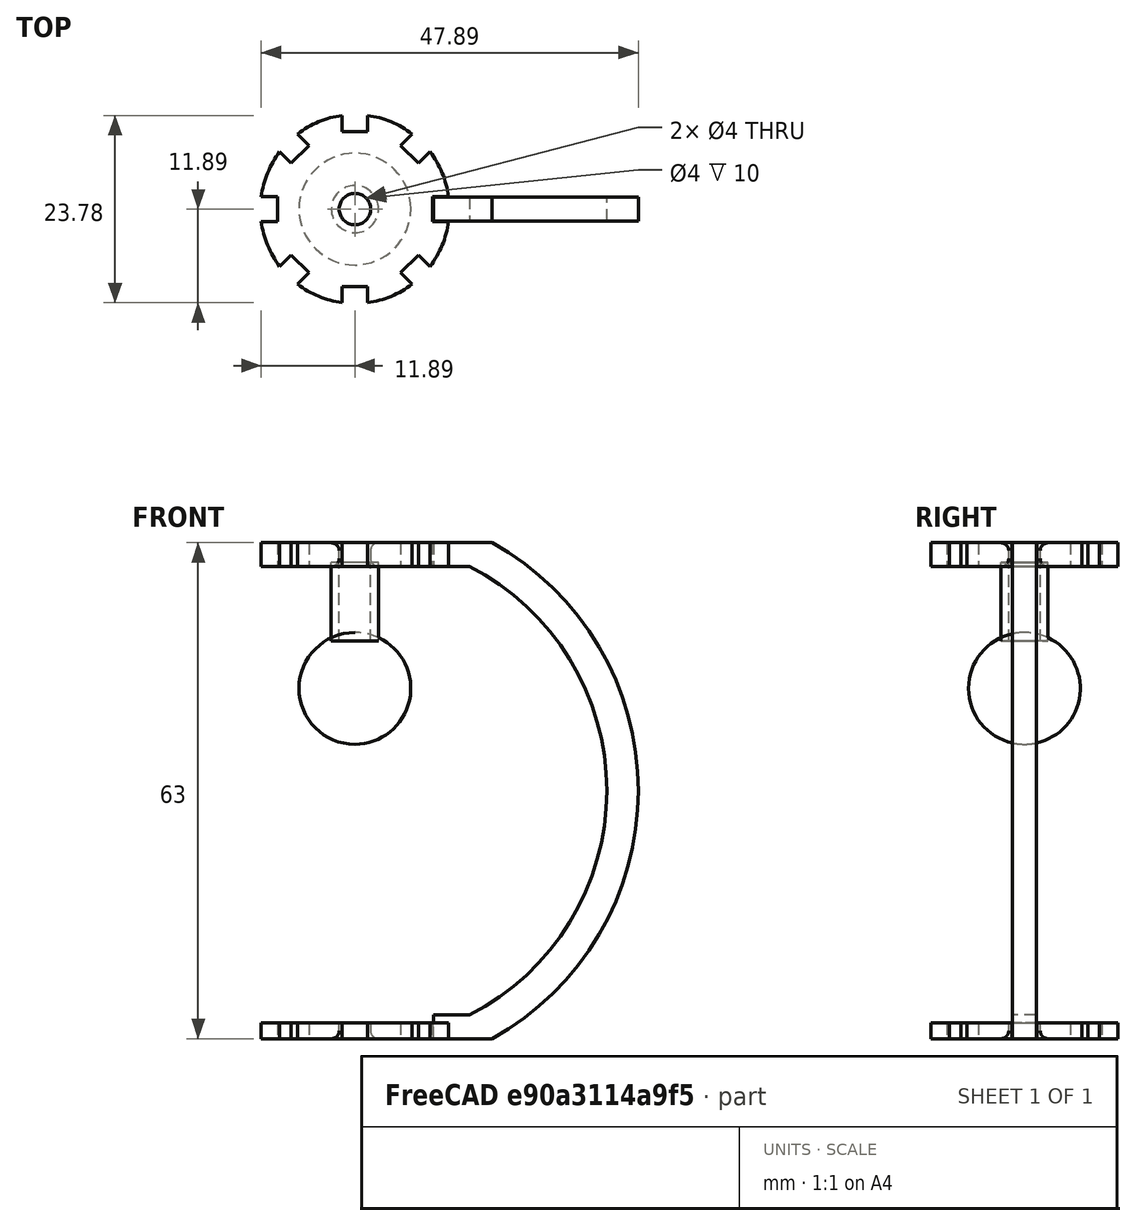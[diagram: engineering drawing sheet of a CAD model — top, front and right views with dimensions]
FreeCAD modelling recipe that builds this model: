
FCSTD DOCUMENT  (FreeCAD 0.19R)
Label: Lamp shade
License: All rights reserved
LicenseURL: http://en.wikipedia.org/wiki/All_rights_reserved
objects: TechDraw::DrawViewDimension×14, TechDraw::DrawProjGroupItem×9, Sketcher::SketchObject×7, PartDesign::Pocket×4, PartDesign::Pad×3, PartDesign::Body×3, PartDesign::Fillet×3, TechDraw::DrawSVGTemplate×2, TechDraw::DrawProjGroup×2, TechDraw::DrawViewSymbol×2, TechDraw::DrawPage×2, PartDesign::PolarPattern×2, Part::FeaturePython×2, TechDraw::DrawViewPart×1, Part::Sphere×1, Part::Compound×1
note: 35 computed .brp shape members not serialized (recipe doc carries the construction recipe); baked Part::Feature solids carry a one-line shape summary decoded from their .brp

FEATURE [Sketcher::SketchObject] Sketch
  FullyConstrained = false
  MapMode = 5
  Placement = pos=(0,0,0) rot=(1,0,0;1.5708rad)
  Support = -> [XZ_Plane]
  sketch-geometry (11):
    g0: LineSegment StartX=0 StartY=31.5 StartZ=0 EndX=10 EndY=31.5 EndZ=0
    g1: LineSegment StartX=0 StartY=-31.5 StartZ=0 EndX=10 EndY=-31.5 EndZ=0
    g2: LineSegment StartX=10 StartY=31.5 StartZ=0 EndX=10 EndY=28.5 EndZ=0
    g3: LineSegment StartX=10 StartY=-31.5 StartZ=0 EndX=10 EndY=-28.5 EndZ=0
    g4: ArcOfCircle CenterX=0 CenterY=0 CenterZ=0 NormalX=0 NormalY=0 NormalZ=1 AngleXU=0 Radius=36 StartAngle=5.21775 EndAngle=7.34862
    g5: LineSegment StartX=10 StartY=31.5 StartZ=0 EndX=17.4284 EndY=31.5 EndZ=0
    g6: LineSegment StartX=17.4284 StartY=-31.5 StartZ=0 EndX=10 EndY=-31.5 EndZ=0
    g7: ArcOfCircle CenterX=0 CenterY=0 CenterZ=0 NormalX=0 NormalY=0 NormalZ=1 AngleXU=0 Radius=32 StartAngle=5.18447 EndAngle=7.3819
    g8: LineSegment StartX=10 StartY=28.5 StartZ=0 EndX=14.5516 EndY=28.5 EndZ=0
    g9: LineSegment StartX=10 StartY=-28.5 StartZ=0 EndX=14.5516 EndY=-28.5 EndZ=0
    g10: LineSegment StartX=0 StartY=15.8658 StartZ=0 EndX=0 EndY=-16.2724 EndZ=0
  constraints (31):
    c: PointOnObject(g0,g-2)
    c: Horizontal(g0)
    c: Horizontal(g1)
    c: DistanceY(g1,g0) = 63
    c: Symmetric(g0,g1,g-1)
    c: DistanceX(g0,g0) = 10
    c: Equal(g1,g0)
    c: Coincident(g2,g0)
    c: Vertical(g2)
    c: Coincident(g3,g1)
    c: Vertical(g3)
    c: Coincident(g5,g2)
    c: Coincident(g5,g4)
    c: Horizontal(g5)
    c: Coincident(g6,g4)
    c: Coincident(g6,g3)
    c: Horizontal(g6)
    c: Coincident(g8,g2)
    c: Coincident(g8,g7)
    c: Coincident(g9,g3)
    c: Coincident(g9,g7)
    c: Horizontal(g9)
    c: Horizontal(g8)
    c: DistanceY(g2,g2) = 3
    c: Equal(g2,g3)
    c: Coincident(g4,g-1)
    c: Coincident(g7,g4)
    c: Radius(g7) = 32
    c: Radius(g4) = 36
    c: PointOnObject(g10,g-2)
    c: Vertical(g10)
FEATURE [PartDesign::Pad] Pad
  Direction = (1,1,1)
  Length = 3
  Length2 = 100
  Midplane = true
  Placement = pos=(0,0,0) rot=(1,0,0;1.5708rad)
  Profile = -> Sketch
  Type = 0
FEATURE [PartDesign::Body] Body  label="Fins"
  Group = -> [Sketch,Pad]
  Origin = -> Origin
  Tip = -> Pad
FEATURE [TechDraw::DrawSVGTemplate] Template
  EditableTexts = Designed_by_Name=MD Harrington; Drawing_number=Drawing number; FC-Date=14/12/22; FC-SC=1:3; FC-SH=Sheet; FC-Title=Title; Subtitle=Light Shade Fins; Weight=Weight
  Height = 210
  Orientation = 1
  Width = 297
FEATURE [TechDraw::DrawProjGroupItem] ProjItem  label="Front"
  CoarseView = false
  Direction = (0,-1,0)
  Focus = 100
  HardHidden = false
  IsoCount = 0
  IsoHidden = false
  IsoVisible = false
  LockPosition = true
  Perspective = false
  Rotation = 0
  RotationVector = (1,0,0)
  ScaleType = 2
  SeamHidden = false
  SeamVisible = true
  SmoothHidden = false
  SmoothVisible = true
  Source = -> [Pad]
  Type = 0
  X = 0
  XDirection = (1,0,0)
  Y = 0
FEATURE [TechDraw::DrawProjGroupItem] ProjItem001  label="Bottom"
  CoarseView = false
  Direction = (0,0,-1)
  Focus = 100
  HardHidden = false
  IsoCount = 0
  IsoHidden = false
  IsoVisible = false
  LockPosition = false
  Perspective = false
  Rotation = 0
  RotationVector = (1,0,0)
  ScaleType = 2
  SeamHidden = false
  SeamVisible = true
  SmoothHidden = false
  SmoothVisible = true
  Source = -> [Pad]
  Type = 5
  X = 0
  XDirection = (1,0,0)
  Y = 65
FEATURE [TechDraw::DrawProjGroupItem] ProjItem002  label="Right"
  CoarseView = false
  Direction = (1,-1e-16,0)
  Focus = 100
  HardHidden = false
  IsoCount = 0
  IsoHidden = false
  IsoVisible = false
  LockPosition = false
  Perspective = false
  Rotation = 0
  RotationVector = (1,0,0)
  ScaleType = 2
  SeamHidden = false
  SeamVisible = true
  SmoothHidden = false
  SmoothVisible = true
  Source = -> [Pad]
  Type = 2
  X = -54.5
  XDirection = (1e-16,1,0)
  Y = 0
FEATURE [TechDraw::DrawProjGroupItem] ProjItem003  label="Left"
  CoarseView = false
  Direction = (-1,-1e-16,0)
  Focus = 100
  HardHidden = false
  IsoCount = 0
  IsoHidden = false
  IsoVisible = false
  LockPosition = false
  Perspective = false
  Rotation = 0
  RotationVector = (1,0,0)
  ScaleType = 2
  SeamHidden = false
  SeamVisible = true
  SmoothHidden = false
  SmoothVisible = true
  Source = -> [Pad]
  Type = 1
  X = 54.5
  XDirection = (1e-16,-1,0)
  Y = 0
FEATURE [TechDraw::DrawProjGroupItem] ProjItem004  label="Rear"
  CoarseView = false
  Direction = (0,1,0)
  Focus = 100
  HardHidden = false
  IsoCount = 0
  IsoHidden = false
  IsoVisible = false
  LockPosition = false
  Perspective = false
  Rotation = 0
  RotationVector = (1,0,0)
  ScaleType = 2
  SeamHidden = false
  SeamVisible = true
  SmoothHidden = false
  SmoothVisible = true
  Source = -> [Pad]
  Type = 3
  X = 120.5
  XDirection = (-1,0,0)
  Y = 0
FEATURE [TechDraw::DrawProjGroup] ProjGroup
  Anchor = -> ProjItem
  AutoDistribute = true
  LockPosition = false
  ProjectionType = 0
  Rotation = 0
  ScaleType = 0
  Source = -> [Pad]
  Views = -> [ProjItem,ProjItem001,ProjItem002,ProjItem003,ProjItem004]
  X = 122.234
  Y = 109.949
  spacingX = 40
  spacingY = 32
FEATURE [TechDraw::DrawViewDimension] Dimension
  Arbitrary = false
  ArbitraryTolerances = false
  EqualTolerance = true
  FormatSpec = %.2f
  FormatSpecOverTolerance = %+.2f
  FormatSpecUnderTolerance = %+.2f
  Inverted = false
  LockPosition = false
  MeasureType = 1
  OverTolerance = 0
  References2D = -> [ProjItem002]
  Rotation = 0
  ScaleType = 0
  TheoreticalExact = false
  Type = 2
  UnderTolerance = 0
  X = -29.0365
  Y = 0
FEATURE [TechDraw::DrawViewDimension] Dimension001
  Arbitrary = false
  ArbitraryTolerances = false
  EqualTolerance = true
  FormatSpec = %.2f
  FormatSpecOverTolerance = %+.2f
  FormatSpecUnderTolerance = %+.2f
  Inverted = false
  LockPosition = false
  MeasureType = 1
  OverTolerance = 0
  References2D = -> [ProjItem]
  Rotation = 0
  ScaleType = 0
  TheoreticalExact = false
  Type = 2
  UnderTolerance = 0
  X = -35.4698
  Y = -0.440584
FEATURE [TechDraw::DrawViewDimension] Dimension002
  Arbitrary = false
  ArbitraryTolerances = false
  EqualTolerance = true
  FormatSpec = %.2f
  FormatSpecOverTolerance = %+.2f
  FormatSpecUnderTolerance = %+.2f
  Inverted = false
  LockPosition = false
  MeasureType = 1
  OverTolerance = 0
  References2D = -> [ProjItem003]
  Rotation = 0
  ScaleType = 0
  TheoreticalExact = false
  Type = 2
  UnderTolerance = 0
  X = 16.4799
  Y = 11.4955
FEATURE [TechDraw::DrawViewDimension] Dimension003
  Arbitrary = false
  ArbitraryTolerances = false
  EqualTolerance = true
  FormatSpec = %.2f
  FormatSpecOverTolerance = %+.2f
  FormatSpecUnderTolerance = %+.2f
  Inverted = false
  LockPosition = false
  MeasureType = 1
  OverTolerance = 0
  References2D = -> [ProjItem003]
  Rotation = 0
  ScaleType = 0
  TheoreticalExact = false
  Type = 1
  UnderTolerance = 0
  X = -32.6032
  Y = 49.3437
FEATURE [TechDraw::DrawViewDimension] Dimension004
  Arbitrary = false
  ArbitraryTolerances = false
  EqualTolerance = true
  FormatSpec = %.2f
  FormatSpecOverTolerance = %+.2f
  FormatSpecUnderTolerance = %+.2f
  Inverted = false
  LockPosition = false
  MeasureType = 1
  OverTolerance = 0
  References2D = -> [ProjItem]
  Rotation = 0
  ScaleType = 0
  TheoreticalExact = false
  Type = 1
  UnderTolerance = 0
  X = -38.144
  Y = 48.6828
FEATURE [TechDraw::DrawViewDimension] Dimension005
  Arbitrary = false
  ArbitraryTolerances = false
  EqualTolerance = true
  FormatSpec = %.2f
  FormatSpecOverTolerance = %+.2f
  FormatSpecUnderTolerance = %+.2f
  Inverted = false
  LockPosition = false
  MeasureType = 1
  OverTolerance = 0
  References2D = -> [ProjItem]
  Rotation = 0
  ScaleType = 0
  TheoreticalExact = false
  Type = 1
  UnderTolerance = 0
  X = -23.0605
  Y = 4.98439
FEATURE [TechDraw::DrawViewDimension] Dimension006
  Arbitrary = false
  ArbitraryTolerances = false
  EqualTolerance = true
  FormatSpec = %.2f
  FormatSpecOverTolerance = %+.2f
  FormatSpecUnderTolerance = %+.2f
  Inverted = false
  LockPosition = false
  MeasureType = 1
  OverTolerance = 0
  References2D = -> [ProjItem001]
  Rotation = 0
  ScaleType = 0
  TheoreticalExact = false
  Type = 1
  UnderTolerance = 0
  X = -60.5803
  Y = 13.1755
FEATURE [TechDraw::DrawViewDimension] Dimension007
  Arbitrary = false
  ArbitraryTolerances = false
  EqualTolerance = true
  FormatSpec = R%.2f
  FormatSpecOverTolerance = %+.2f
  FormatSpecUnderTolerance = %+.2f
  Inverted = false
  LockPosition = false
  MeasureType = 1
  OverTolerance = 0
  References2D = -> [ProjItem004]
  Rotation = 0
  ScaleType = 0
  TheoreticalExact = false
  Type = 4
  UnderTolerance = 0
  X = -15.2002
  Y = 52.2092
FEATURE [TechDraw::DrawViewDimension] Dimension008
  Arbitrary = false
  ArbitraryTolerances = false
  EqualTolerance = true
  FormatSpec = R%.2f
  FormatSpecOverTolerance = %+.2f
  FormatSpecUnderTolerance = %+.2f
  Inverted = false
  LockPosition = false
  MeasureType = 1
  OverTolerance = 0
  References2D = -> [ProjItem004]
  Rotation = 0
  ScaleType = 0
  TheoreticalExact = false
  Type = 4
  UnderTolerance = 0
  X = -29.0785
  Y = -21.148
FEATURE [TechDraw::DrawViewPart] View
  CoarseView = false
  Direction = (0,-1,0)
  Focus = 100
  HardHidden = false
  IsoCount = 0
  IsoHidden = false
  IsoVisible = false
  LockPosition = false
  Perspective = false
  Rotation = 0
  ScaleType = 0
  SeamHidden = false
  SeamVisible = true
  SmoothHidden = false
  SmoothVisible = true
  Source = -> [Dimension008]
  X = 148.5
  XDirection = (1,0,0)
  Y = 105
FEATURE [TechDraw::DrawViewSymbol] ActiveView
  LockPosition = false
  Rotation = 0
  ScaleType = 2
  Symbol = <blob: 55645 chars omitted>
  X = 268.703
  Y = 156.462
FEATURE [TechDraw::DrawPage] Page  label="FinsTecDrawing"
  KeepUpdated = true
  NextBalloonIndex = 1
  ProjectionType = 0
  Template = -> Template
  Views = -> [ProjGroup,Dimension,Dimension001,Dimension002,Dimension003,Dimension004,Dimension005,Dimension006,Dimension007,Dimension008,View,ActiveView]
FEATURE [Sketcher::SketchObject] Sketch001
  AttachmentOffset = pos=(0,0,28.5) rot=(0,0,1;0rad)
  FullyConstrained = true
  MapMode = 5
  Placement = pos=(0,0,28.5) rot=(0,0,1;0rad)
  Support = -> [XY_Plane001]
  sketch-geometry (1):
    g0: Circle CenterX=0 CenterY=0 CenterZ=0 NormalX=0 NormalY=0 NormalZ=1 AngleXU=0 Radius=12
  constraints (2):
    c: Coincident(g0,g-1)
    c: Radius(g0) = 12
FEATURE [PartDesign::Pad] Pad001
  Direction = (1,1,1)
  Length = 3
  Length2 = 100
  Profile = -> Sketch001
  Type = 0
FEATURE [Sketcher::SketchObject] Sketch002
  FullyConstrained = true
  MapMode = 5
  Placement = pos=(0,0,31.5) rot=(0,0,1;0rad)
  Support = -> [Pad001]
  sketch-geometry (4):
    g0: LineSegment StartX=9.84 StartY=1.6 StartZ=0 EndX=12.41 EndY=1.6 EndZ=0
    g1: LineSegment StartX=12.41 StartY=1.6 StartZ=0 EndX=12.41 EndY=-1.6 EndZ=0
    g2: LineSegment StartX=12.41 StartY=-1.6 StartZ=0 EndX=9.84 EndY=-1.6 EndZ=0
    g3: LineSegment StartX=9.84 StartY=-1.6 StartZ=0 EndX=9.84 EndY=1.6 EndZ=0
  constraints (11):
    c: Coincident(g0,g1)
    c: Coincident(g1,g2)
    c: Coincident(g2,g3)
    c: Coincident(g3,g0)
    c: Horizontal(g0)
    c: Horizontal(g2)
    c: Vertical(g1)
    c: DistanceY(g3,g3) = 3.2
    c: Symmetric(g0,g2,g-1)
    c: DistanceX(g0,g0) = 2.57
    c: DistanceX(g-1,g0) = 9.84
FEATURE [PartDesign::Pocket] Pocket
  BaseFeature = -> Pad001
  Length = 5
  Length2 = 100
  Profile = -> Sketch002
  Type = 0
FEATURE [PartDesign::PolarPattern] PolarPattern
  Angle = 360
  Axis = -> Sketch002 [N_Axis]
  BaseFeature = -> Pocket
  Occurrences = 8
  Originals = -> [Pocket]
FEATURE [Sketcher::SketchObject] Sketch003
  FullyConstrained = true
  MapMode = 5
  Placement = pos=(0,0,31.5) rot=(0,0,1;0rad)
  Support = -> [PolarPattern]
  sketch-geometry (1):
    g0: Circle CenterX=0 CenterY=0 CenterZ=0 NormalX=0 NormalY=0 NormalZ=1 AngleXU=0 Radius=2
  constraints (2):
    c: Coincident(g0,g-1)
    c: Radius(g0) = 2
FEATURE [PartDesign::Pocket] Pocket001
  BaseFeature = -> PolarPattern
  Length = 6
  Length2 = 100
  Profile = -> Sketch003
  Type = 0
FEATURE [PartDesign::Fillet] Fillet
  Base = -> Pocket001 [Edge36]
  BaseFeature = -> Pocket001
  Radius = 1
  SupportTransform = false
FEATURE [Sketcher::SketchObject] Sketch005
  AttachmentOffset = pos=(0,0,28.5) rot=(0,0,1;0rad)
  FullyConstrained = true
  MapMode = 5
  Placement = pos=(0,0,28.5) rot=(0,0,1;0rad)
  Support = -> [XY_Plane002]
  sketch-geometry (1):
    g0: Circle CenterX=0 CenterY=0 CenterZ=0 NormalX=0 NormalY=0 NormalZ=1 AngleXU=0 Radius=12
  constraints (2):
    c: Coincident(g0,g-1)
    c: Radius(g0) = 12
FEATURE [PartDesign::Pad] Pad002
  Direction = (1,1,1)
  Length = 2
  Length2 = 100
  Profile = -> Sketch005
  Type = 0
FEATURE [Sketcher::SketchObject] Sketch004
  FullyConstrained = true
  MapMode = 5
  Placement = pos=(0,0,30.5) rot=(0,0,1;0rad)
  Support = -> [Pad002]
  sketch-geometry (4):
    g0: LineSegment StartX=9.84 StartY=1.6 StartZ=0 EndX=12.41 EndY=1.6 EndZ=0
    g1: LineSegment StartX=12.41 StartY=1.6 StartZ=0 EndX=12.41 EndY=-1.6 EndZ=0
    g2: LineSegment StartX=12.41 StartY=-1.6 StartZ=0 EndX=9.84 EndY=-1.6 EndZ=0
    g3: LineSegment StartX=9.84 StartY=-1.6 StartZ=0 EndX=9.84 EndY=1.6 EndZ=0
  constraints (11):
    c: Coincident(g0,g1)
    c: Coincident(g1,g2)
    c: Coincident(g2,g3)
    c: Coincident(g3,g0)
    c: Horizontal(g0)
    c: Horizontal(g2)
    c: Vertical(g1)
    c: DistanceY(g3,g3) = 3.2
    c: Symmetric(g0,g2,g-1)
    c: DistanceX(g0,g0) = 2.57
    c: DistanceX(g-1,g0) = 9.84
FEATURE [PartDesign::Pocket] Pocket003
  BaseFeature = -> Pad002
  Length = 5
  Length2 = 100
  Profile = -> Sketch004
  Type = 0
FEATURE [PartDesign::PolarPattern] PolarPattern001
  Angle = 360
  Axis = -> Sketch004 [N_Axis]
  BaseFeature = -> Pocket003
  Occurrences = 8
  Originals = -> [Pocket003]
FEATURE [Sketcher::SketchObject] Sketch006
  FullyConstrained = true
  MapMode = 5
  Placement = pos=(0,0,30.5) rot=(0,0,1;0rad)
  Support = -> [PolarPattern001]
  sketch-geometry (1):
    g0: Circle CenterX=0 CenterY=0 CenterZ=0 NormalX=0 NormalY=0 NormalZ=1 AngleXU=0 Radius=2
  constraints (2):
    c: Coincident(g0,g-1)
    c: Radius(g0) = 2
FEATURE [PartDesign::Pocket] Pocket002
  BaseFeature = -> PolarPattern001
  Length = 6
  Length2 = 100
  Profile = -> Sketch006
  Type = 0
FEATURE [PartDesign::Fillet] Fillet001
  Base = -> Pocket002 [Edge36]
  BaseFeature = -> Pocket002
  Radius = 1
  SupportTransform = false
FEATURE [PartDesign::Body] Body002  label="Top001"
  Group = -> [Sketch005,Pad002,Sketch004,Pocket003,PolarPattern001,Sketch006,Pocket002,Fillet001]
  Origin = -> Origin002
  Placement = pos=(0,0,-60) rot=(0,0,1;0rad)
  Tip = -> Fillet001
FEATURE [PartDesign::Fillet] Fillet002
  Base = -> Fillet [Edge101]
  BaseFeature = -> Fillet
  Radius = 1
  SupportTransform = false
FEATURE [PartDesign::Body] Body001  label="Top"
  Group = -> [Sketch001,Pad001,Sketch002,Pocket,PolarPattern,Sketch003,Pocket001,Fillet,Fillet002]
  Origin = -> Origin001
  Tip = -> Fillet002
FEATURE [Part::FeaturePython] Array  # Draft array (typed FeaturePython)
  Angle = 360
  ArrayType = 1
  Axis = (0,0,1)
  Base = -> Body
  Center = (0,0,0)
  Count = 8
  ExpandArray = false
  Fuse = false
  IntervalAxis = (0,0,0)
  IntervalX = (50,0,0)
  IntervalY = (0,50,0)
  IntervalZ = (0,0,50)
  NumberCircles = 3
  NumberPolar = 8
  NumberX = 2
  NumberY = 2
  NumberZ = 1
  PlacementList = 8 placements: [(0,0,0),(0,0,0),(0,0,0),(0,0,0),(0,0,0),(0,0,0),(0,0,0),(0,0,0)]
  RadialDistance = 50
  ScaleList = (8) [(1,1,1),(1,1,1),(1,1,1),(1,1,1),(1,1,1),(1,1,1),(1,1,1),(1,1,1)]
  Symmetry = 1
  TangentialDistance = 25
FEATURE [Part::FeaturePython] Tube  # WARN: FeaturePython — macro-defined, semantics opaque (R4)
  AttacherType = Attacher::AttachEngine3D
  Height = 10
  InnerRadius = 2
  OuterRadius = 3
  Placement = pos=(0,0,19) rot=(0,0,1;0rad)
FEATURE [Part::Sphere] Sphere
  Angle1 = -90
  Angle2 = 90
  Angle3 = 360
  AttacherType = Attacher::AttachEngine3D
  Placement = pos=(0,0,13) rot=(0,0,1;0rad)
  Radius = 7.1
FEATURE [Part::Compound] Compound  label="Lightbulb and holder"
  Links = -> [Tube,Sphere]
FEATURE [TechDraw::DrawSVGTemplate] Template002
  EditableTexts = Designed_by_Name=MD Harrington; Drawing_number=Drawing number; FC-Date=Date; FC-SC=1:3; FC-SH=Sheet; FC-Title=Title; Subtitle=Light Shade Top and Bottom Plates; Weight=Weight
  Height = 210
  Orientation = 1
  Width = 297
FEATURE [TechDraw::DrawProjGroupItem] ProjItem005  label="Front001"
  CoarseView = false
  Direction = (-1,0,0)
  Focus = 100
  HardHidden = false
  IsoCount = 0
  IsoHidden = false
  IsoVisible = false
  LockPosition = true
  Perspective = false
  Rotation = 0
  RotationVector = (0,-1,0)
  ScaleType = 2
  SeamHidden = false
  SeamVisible = true
  SmoothHidden = false
  SmoothVisible = true
  Source = -> [Body001]
  Type = 0
  X = 0
  XDirection = (0,-1,0)
  Y = 0
FEATURE [TechDraw::DrawProjGroupItem] ProjItem006  label="Bottom001"
  CoarseView = false
  Direction = (0,0,-1)
  Focus = 100
  HardHidden = false
  IsoCount = 0
  IsoHidden = false
  IsoVisible = false
  LockPosition = false
  Perspective = false
  Rotation = 0
  RotationVector = (1,0,0)
  ScaleType = 2
  SeamHidden = false
  SeamVisible = true
  SmoothHidden = false
  SmoothVisible = true
  Source = -> [Body001]
  Type = 5
  X = 0
  XDirection = (0,-1,0)
  Y = -28.7857
FEATURE [TechDraw::DrawProjGroupItem] ProjItem007  label="FrontBottomLeft"
  CoarseView = false
  Direction = (-0.57735,0.57735,-0.57735)
  Focus = 100
  HardHidden = false
  IsoCount = 0
  IsoHidden = false
  IsoVisible = false
  LockPosition = false
  Perspective = false
  Rotation = 0
  RotationVector = (1,0,0)
  ScaleType = 2
  SeamHidden = false
  SeamVisible = true
  SmoothHidden = false
  SmoothVisible = true
  Source = -> [Body001]
  Type = 8
  X = -66.7857
  XDirection = (-0.707107,-0.707107,0)
  Y = -32.5875
FEATURE [TechDraw::DrawProjGroupItem] ProjItem008  label="Top002"
  CoarseView = false
  Direction = (0,0,1)
  Focus = 100
  HardHidden = false
  IsoCount = 0
  IsoHidden = false
  IsoVisible = false
  LockPosition = false
  Perspective = false
  Rotation = 0
  RotationVector = (1,0,0)
  ScaleType = 2
  SeamHidden = false
  SeamVisible = true
  SmoothHidden = false
  SmoothVisible = true
  Source = -> [Body001]
  Type = 4
  X = 0
  XDirection = (0,-1,0)
  Y = 28.7857
FEATURE [TechDraw::DrawProjGroup] ProjGroup001
  Anchor = -> ProjItem005
  AutoDistribute = true
  LockPosition = false
  ProjectionType = 1
  Rotation = 0
  ScaleType = 2
  Source = -> [Body001]
  Views = -> [ProjItem005,ProjItem006,ProjItem007,ProjItem008]
  X = 119.113
  Y = 116.358
  spacingX = 43
  spacingY = 5
FEATURE [TechDraw::DrawViewDimension] Dimension009
  Arbitrary = false
  ArbitraryTolerances = false
  EqualTolerance = true
  FormatSpec = R%.2f
  FormatSpecOverTolerance = %+.2f
  FormatSpecUnderTolerance = %+.2f
  Inverted = false
  LockPosition = false
  MeasureType = 1
  OverTolerance = 0
  References2D = -> [ProjItem008]
  Rotation = 0
  ScaleType = 0
  TheoreticalExact = false
  Type = 4
  UnderTolerance = 0
  X = 64.338
  Y = 35.2038
FEATURE [TechDraw::DrawViewDimension] Dimension010
  Arbitrary = false
  ArbitraryTolerances = false
  EqualTolerance = true
  FormatSpec = %.2f
  FormatSpecOverTolerance = %+.2f
  FormatSpecUnderTolerance = %+.2f
  Inverted = false
  LockPosition = false
  MeasureType = 1
  OverTolerance = 0
  References2D = -> [ProjItem008]
  Rotation = 0
  ScaleType = 0
  TheoreticalExact = false
  Type = 0
  UnderTolerance = 0
  X = 49.551
  Y = 14.3639
FEATURE [TechDraw::DrawViewDimension] Dimension011
  Arbitrary = false
  ArbitraryTolerances = false
  EqualTolerance = true
  FormatSpec = %.2f
  FormatSpecOverTolerance = %+.2f
  FormatSpecUnderTolerance = %+.2f
  Inverted = false
  LockPosition = false
  MeasureType = 1
  OverTolerance = 0
  References2D = -> [ProjItem008]
  Rotation = 0
  ScaleType = 0
  TheoreticalExact = false
  Type = 2
  UnderTolerance = 0
  X = -55.7668
  Y = -17.1973
FEATURE [TechDraw::DrawViewDimension] Dimension013
  Arbitrary = false
  ArbitraryTolerances = false
  EqualTolerance = true
  FormatSpec = R%.2f
  FormatSpecOverTolerance = %+.2f
  FormatSpecUnderTolerance = %+.2f
  Inverted = false
  LockPosition = false
  MeasureType = 1
  OverTolerance = 0
  References2D = -> [ProjItem006]
  Rotation = 0
  ScaleType = 0
  TheoreticalExact = false
  Type = 4
  UnderTolerance = 0
  X = 16.3224
  Y = 14.819
FEATURE [TechDraw::DrawViewDimension] Dimension014
  Arbitrary = false
  ArbitraryTolerances = false
  EqualTolerance = true
  FormatSpec = R%.2f
  FormatSpecOverTolerance = %+.2f
  FormatSpecUnderTolerance = %+.2f
  Inverted = false
  LockPosition = false
  MeasureType = 1
  OverTolerance = 0
  References2D = -> [ProjItem006]
  Rotation = 0
  ScaleType = 0
  TheoreticalExact = false
  Type = 4
  UnderTolerance = 0
  X = -19.7229
  Y = 15.7497
FEATURE [TechDraw::DrawViewSymbol] ActiveView001
  LockPosition = false
  Rotation = 0
  ScaleType = 2
  Symbol = <blob: 262729 chars omitted>
  X = 252.25
  Y = 125.548
FEATURE [TechDraw::DrawPage] Page002  label="Light Shade Top - Bottom Plates"
  KeepUpdated = true
  NextBalloonIndex = 1
  ProjectionType = 0
  Template = -> Template002
  Views = -> [ProjGroup001,Dimension009,Dimension010,Dimension011,Dimension013,Dimension014,ActiveView001]
